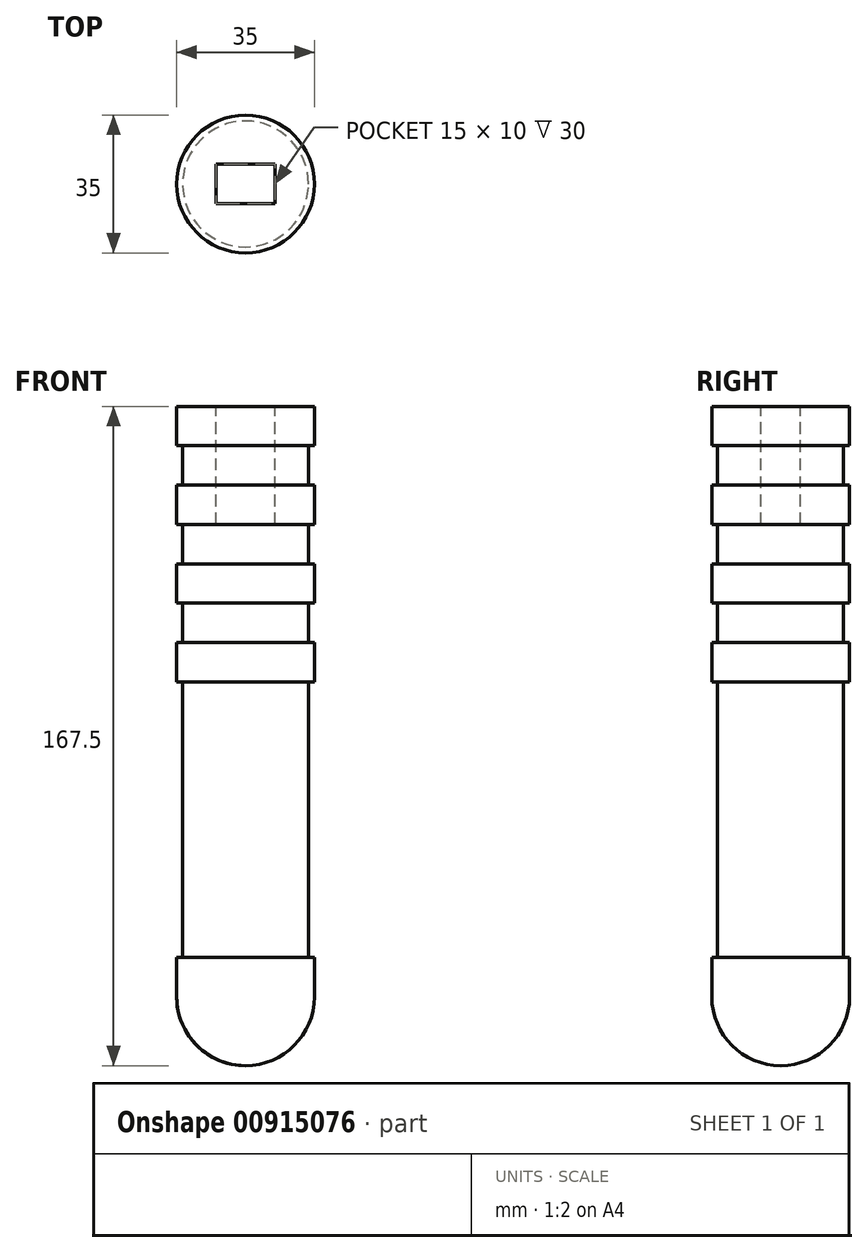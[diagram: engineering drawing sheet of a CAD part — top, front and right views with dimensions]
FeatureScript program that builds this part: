
annotation { "Feature Type Name" : "Feature", "Feature Type Description" : "" }
export const myFeature = defineFeature(function(context is Context, id is Id, definition is map)
    precondition{}
    {
        {
            var Q0;
            Q0=qCreatedBy(makeId("Front.planeOp"),FACE);
            var sketch = newSketch(context, id + "F0", { "sketchPlane" : qUnion([Q0])});
            skLineSegment(sketch, "E0", {"start": v(0, 0) * mm, "end": v(0, 150) * mm});
            skLineSegment(sketch, "E1", {"start": v(0, 150) * mm, "end": v(17.5, 150) * mm});
            skLineSegment(sketch, "E2", {"start": v(17.5, 150) * mm, "end": v(17.5, 140) * mm});
            skLineSegment(sketch, "E3", {"start": v(17.5, 140) * mm, "end": v(16, 140) * mm});
            skLineSegment(sketch, "E4", {"start": v(16, 140) * mm, "end": v(16, 130) * mm});
            skLineSegment(sketch, "E5", {"start": v(16, 130) * mm, "end": v(17.5, 130) * mm});
            skLineSegment(sketch, "E6", {"start": v(17.5, 130) * mm, "end": v(17.5, 120) * mm});
            skLineSegment(sketch, "E7", {"start": v(17.5, 120) * mm, "end": v(16, 120) * mm});
            skLineSegment(sketch, "E8", {"start": v(16, 120) * mm, "end": v(16, 110) * mm});
            skLineSegment(sketch, "E9", {"start": v(16, 110) * mm, "end": v(17.5, 110) * mm});
            skLineSegment(sketch, "E10", {"start": v(17.5, 110) * mm, "end": v(17.5, 100) * mm});
            skLineSegment(sketch, "E11", {"start": v(17.5, 100) * mm, "end": v(16, 100) * mm});
            skLineSegment(sketch, "E12", {"start": v(16, 100) * mm, "end": v(16, 90) * mm});
            skLineSegment(sketch, "E13", {"start": v(16, 90) * mm, "end": v(17.5, 90) * mm});
            skLineSegment(sketch, "E14", {"start": v(17.5, 90) * mm, "end": v(17.5, 80) * mm});
            skLineSegment(sketch, "E15", {"start": v(17.5, 80) * mm, "end": v(16, 80) * mm});
            skLineSegment(sketch, "E16", {"start": v(16, 80) * mm, "end": v(16, 10) * mm});
            skLineSegment(sketch, "E17", {"start": v(16, 10) * mm, "end": v(17.5, 10) * mm});
            skLineSegment(sketch, "E18", {"start": v(17.5, 10) * mm, "end": v(17.5, 0) * mm});
            skLineSegment(sketch, "E19", {"start": v(17.5, 0) * mm, "end": v(0, 0) * mm});
            skArc(sketch, "E20", {"start": v(17.5, 0) * mm, "mid": v(12.37, -12.37) * mm, "end": v(0, -17.5) * mm});
            skLineSegment(sketch, "E21", {"start": v(0, 0) * mm, "end": v(0, -17.5) * mm});
            skSolve(sketch);
        }
        {
            var Q0;
            Q0=makeQuery(id+"F0.imprint","IMPRINT",FACE,{"disambiguationData":[TD([[makeQuery(id+"F0.imprint","IMPRINT",EDGE,{"derivedFrom":sQuery(id+"F0.wireOp",EDGE,"E19")}),1.0]])]});
            var Q1;
            Q1=makeQuery(id+"F0.imprint","IMPRINT",FACE,{"disambiguationData":[TD([[makeQuery(id+"F0.imprint","IMPRINT",EDGE,{"derivedFrom":sQuery(id+"F0.wireOp",EDGE,"E0")}),-1.0]])]});
            var Q2;
            Q2=sQuery(id+"F0.wireOp",EDGE,"E0");
            revolve(context, id + "F1", {"surfaceOperationType" : NewSurfaceOperationType.NEW, "entities" : qUnion([Q0, Q1]), "axis" : qUnion([Q2]), "revolveType" : RevolveType.FULL});
        }
        {
            var Q0;
            Q0=makeQuery(id+"F1.opRevolve","SWEPT_FACE",FACE,{"disambiguationData":[OSD([sQuery(id+"F0.wireOp",EDGE,"E1")])]});
            var sketch = newSketch(context, id + "F2", { "sketchPlane" : qUnion([Q0])});
            skLineSegment(sketch, "E22.bottom", {"start": v(7.5, -5) * mm, "end": v(-7.5, -5) * mm});
            skLineSegment(sketch, "E22.top", {"start": v(7.5, 5) * mm, "end": v(-7.5, 5) * mm});
            skLineSegment(sketch, "E22.left", {"start": v(7.5, -5) * mm, "end": v(7.5, 5) * mm});
            skLineSegment(sketch, "E22.right", {"start": v(-7.5, -5) * mm, "end": v(-7.5, 5) * mm});
            skPoint(sketch, "E22.middle", {"position": v(0, 0) * mm});
            skSolve(sketch);
        }
        {
            var Q0;
            Q0 = qSketchRegion(id + "F2", true);
            extrude(context, id + "F3", {"entities" : qUnion([Q0]), "operationType" : NewBodyOperationType.REMOVE, "oppositeDirection" : true, "depth" : 30 * mm, "offsetDistance" : 25 * mm});
        }
    });
